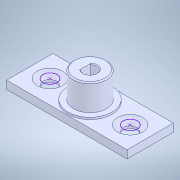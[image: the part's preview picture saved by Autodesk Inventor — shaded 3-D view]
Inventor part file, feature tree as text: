
AUTODESK INVENTOR PART (.ipt)
format: ipt  version: 2021 (Build 250183000, 183)  size: 169,984 bytes
history: native  units: in
note: dims shown in document units (in); Inventor stores cm internally (conversion verified against a paired STEP export)
features: sketch x5, extrude x4, chamfer x2, projected_geometry x2, hole x1, other x1
ambient origin geometry x8: Origin, YZ Plane, XZ Plane, XY Plane, X Axis, Y Axis, Z Axis, Center Point
bodies: Solid1 (feature_tree)
feature tree (15):
  extrude  "Extrusion1"  Depth=0.3937in TaperAngle=0.0deg
  extrude  "Extrusion2"  Depth=0.3937in TaperAngle=0.0deg
  extrude  "Extrusion3"  Depth=0.002in
  extrude  "Extrusion4"  Depth=0.3937in TaperAngle=45.0deg
  chamfer  "Chamfer1"  Distance=0.3937in
  hole  "Hole2"  [1 undecoded]
  chamfer  "Chamfer2"  [1 undecoded]
  sketch  "Sketch1"  dims[d1=0.3937in d2=0.0in d3=0.3937in d4=0.0in]
  projected_geometry  "Projected Loop1"
  sketch  "Sketch2"  dims[d5=0.0039in d6=0.3937in d7=0.0in]
  sketch  "Sketch3"  dims[d8=0.0118in d9=0.0787in d10=45.0deg]
  sketch  "Sketch6"  dims[d19=0.1339in d20=0.2362in d21=0.248in d22=0.0787in d23=90.0deg d24=0.315in d25=0.0in d26=0.002in]
  sketch  "Sketch7"  dims[d27=0.002in d28=0.0079in d29=0.0787in d30=45.0deg d32=0.3937in d33=0.0in d34=0.0039in]
  projected_geometry  "Projected Loop2"
  other  "CSK for M4 Countersunk Flat Head Screw1"
note: 2 required parameter values undecoded (feature->parameter linkage not recoverable at this tier; creation-order binding heuristic only, values carry confidence <= 0.55)
